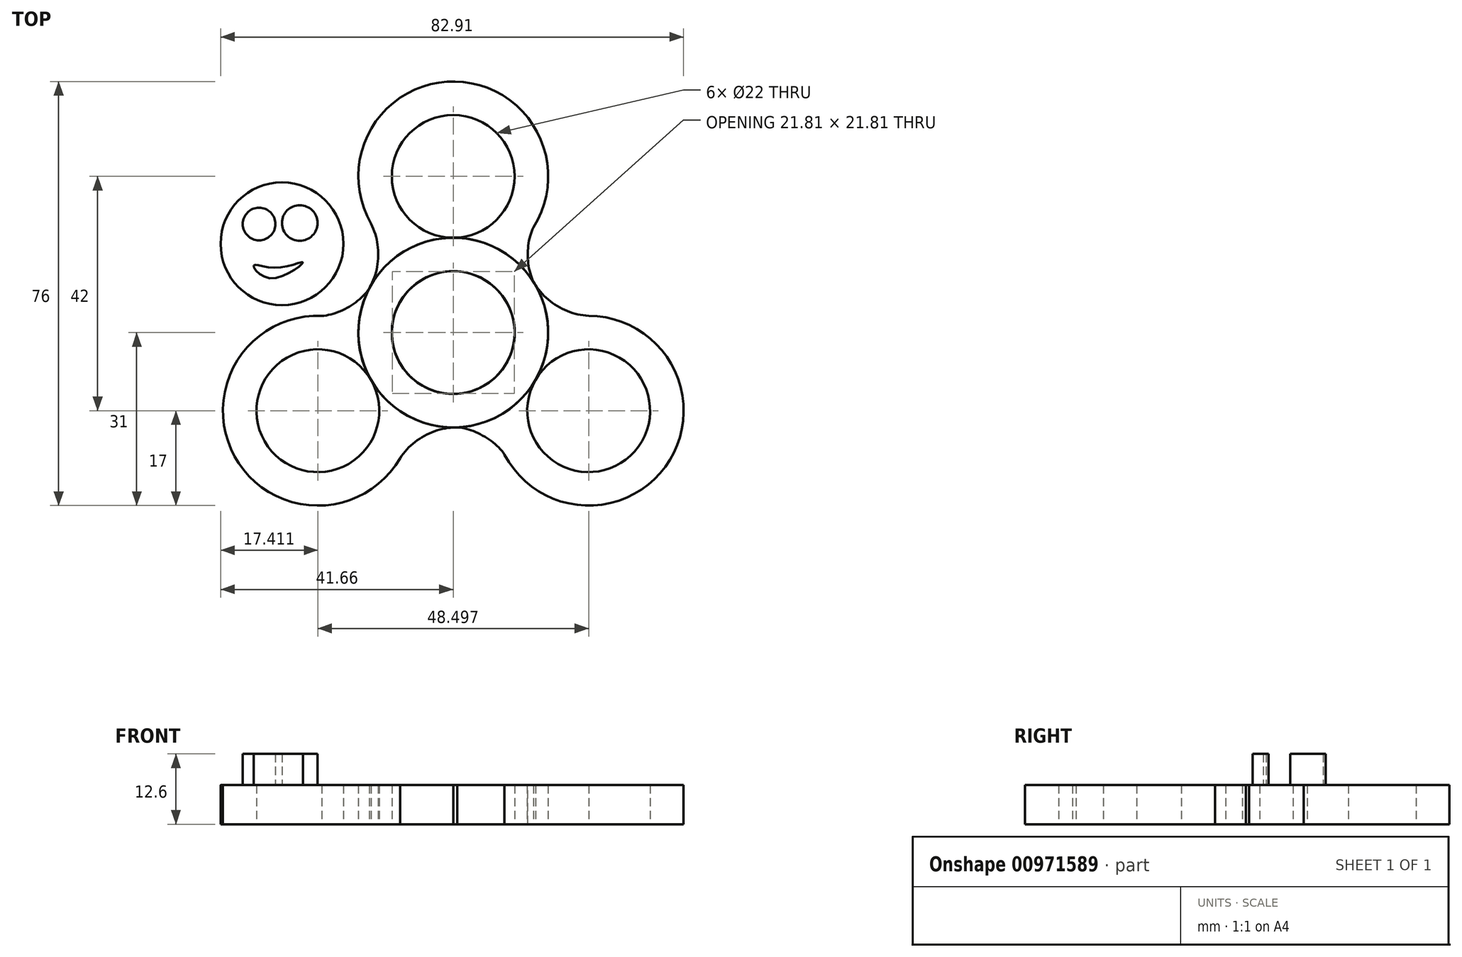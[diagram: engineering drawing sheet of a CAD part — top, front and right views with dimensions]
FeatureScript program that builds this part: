
annotation { "Feature Type Name" : "Feature", "Feature Type Description" : "" }
export const myFeature = defineFeature(function(context is Context, id is Id, definition is map)
    precondition{}
    {
        {
            var Q0;
            Q0=qCreatedBy(makeId("Top.planeOp"),FACE);
            var sketch = newSketch(context, id + "F0", { "sketchPlane" : qUnion([Q0])});
            skArc(sketch, "E0", {"start": v(-14.72, 8.5) * mm, "mid": v(0.36, -17) * mm, "end": v(14.35, 9.1) * mm});
            skArc(sketch, "E1", {"start": v(14.35, 18.9) * mm, "mid": v(0.36, 45) * mm, "end": v(-14.72, 19.5) * mm});
            skFitSpline(sketch, "E2", {"points": [v(-14.72, 19.5) * mm, v(-14.72, 8.5) * mm], "startDerivative": vector(5.17, -10.15) * mm, "endDerivative": vector(-5.17, -10.15) * mm});
            skFitSpline(sketch, "E3", {"points": [v(14.35, 18.9) * mm, v(14.35, 9.1) * mm], "startDerivative": vector(-4.06, -8.32) * mm, "endDerivative": vector(4.06, -8.32) * mm});
            skSolve(sketch);
        }
        {
            var Q0;
            Q0=makeQuery(id+"F0.imprint","IMPRINT",FACE,{"disambiguationData":[TD([[makeQuery(id+"F0.imprint","IMPRINT",EDGE,{"derivedFrom":sQuery(id+"F0.wireOp",EDGE,"E0")}),1.0]])]});
            extrude(context, id + "F1", {"entities" : qUnion([Q0]), "depth" : 7 * mm, "offsetDistance" : 25 * mm});
        }
        {
            var Q0;
            Q0=makeQuery(id+"F1.opExtrude","CAP_FACE",FACE,{"disambiguationData":[OSD([sQuery(id+"F0.wireOp",EDGE,"E0"),sQuery(id+"F0.wireOp",EDGE,"E1"),sQuery(id+"F0.wireOp",EDGE,"E2"),sQuery(id+"F0.wireOp",EDGE,"E3")])],"isStart":true});
            var sketch = newSketch(context, id + "F2", { "sketchPlane" : qUnion([Q0])});
            skCircle(sketch, "E4", {"center": v(0, 0) * mm, "radius": 11 * mm});
            skCircle(sketch, "E5", {"center": v(0, -28) * mm, "radius": 11 * mm});
            skSolve(sketch);
        }
        {
            var Q0;
            Q0 = qSketchRegion(id + "F2", true);
            extrude(context, id + "F3", {"entities" : qUnion([Q0]), "operationType" : NewBodyOperationType.REMOVE, "oppositeDirection" : true, "depth" : 25 * mm, "offsetDistance" : 25 * mm});
        }
        {
            var Q0;
            Q0=makeQuery(id+"F1.opExtrude","SWEPT_BODY",BODY,{"disambiguationData":[OSD([sQuery(id+"F0.wireOp",EDGE,"E0"),sQuery(id+"F0.wireOp",EDGE,"E1"),sQuery(id+"F0.wireOp",EDGE,"E2"),sQuery(id+"F0.wireOp",EDGE,"E3")])]});
            var Q1;
            Q1=makeQuery(id+"F3.boolean.opBoolean","INTERSECT",EDGE,{"derivedFrom":[makeQuery(id+"F1.opExtrude","CAP_FACE",FACE,{"disambiguationData":[OSD([sQuery(id+"F0.wireOp",EDGE,"E0"),sQuery(id+"F0.wireOp",EDGE,"E1"),sQuery(id+"F0.wireOp",EDGE,"E2"),sQuery(id+"F0.wireOp",EDGE,"E3")])],"isStart":false}),makeQuery(id+"F3.opExtrude","SWEPT_FACE",FACE,{"disambiguationData":[OSD([sQuery(id+"F2.wireOp",EDGE,"E4")])]})]});
            circularPattern(context, id + "F4", {"entities" : qUnion([Q0]), "axis" : qUnion([Q1]), "angle" : 360 * degree, "instanceCount" : 3, "equalSpace" : true});
        }
        {
            var Q0;
            Q0=qCreatedBy(makeId("Top.planeOp"),FACE);
            var sketch = newSketch(context, id + "F5", { "sketchPlane" : qUnion([Q0])});
            skCircle(sketch, "E6", {"center": v(-53.46, 44.5) * mm, "radius": 11 * mm});
            skSolve(sketch);
        }
        {
            var Q0;
            Q0=makeQuery(id+"F5.imprint","IMPRINT",FACE,{"disambiguationData":[TD([[makeQuery(id+"F5.imprint","IMPRINT",EDGE,{"derivedFrom":sQuery(id+"F5.wireOp",EDGE,"E6")}),1.0]])]});
            extrude(context, id + "F6", {"entities" : qUnion([Q0]), "depth" : 7 * mm, "offsetDistance" : 25 * mm});
        }
        {
            var Q0;
            Q0=makeQuery(id+"F6.opExtrude","CAP_FACE",FACE,{"disambiguationData":[OSD([sQuery(id+"F5.wireOp",EDGE,"E6")])],"isStart":false});
            var sketch = newSketch(context, id + "F7", { "sketchPlane" : qUnion([Q0])});
            skCircle(sketch, "E7", {"center": v(-57.57, 48.05) * mm, "radius": 2.92 * mm});
            skCircle(sketch, "E8", {"center": v(-50.3, 48.24) * mm, "radius": 3.2 * mm});
            skFitSpline(sketch, "E9", {"points": [v(-58.5, 40.59) * mm, v(-55.52, 38.35) * mm, v(-49.73, 41.15) * mm, v(-54.4, 40.21) * mm, v(-58.5, 40.59) * mm]});
            skSolve(sketch);
        }
        {
            var Q0;
            Q0=makeQuery(id+"F7.imprint","IMPRINT",FACE,{"disambiguationData":[TD([[makeQuery(id+"F7.imprint","IMPRINT",EDGE,{"derivedFrom":sQuery(id+"F7.wireOp",EDGE,"E7")}),1.0]])]});
            var Q1;
            Q1=makeQuery(id+"F7.imprint","IMPRINT",FACE,{"disambiguationData":[TD([[makeQuery(id+"F7.imprint","IMPRINT",EDGE,{"derivedFrom":sQuery(id+"F7.wireOp",EDGE,"E8")}),1.0]])]});
            var Q2;
            Q2=makeQuery(id+"F7.imprint","IMPRINT",FACE,{"disambiguationData":[TD([[makeQuery(id+"F7.imprint","IMPRINT",EDGE,{"derivedFrom":sQuery(id+"F7.wireOp",EDGE,"E9")}),1.0]])]});
            extrude(context, id + "F8", {"entities" : qUnion([Q0, Q1, Q2]), "operationType" : NewBodyOperationType.ADD, "depth" : 5.6 * mm, "offsetDistance" : 25 * mm});
        }
        {
            var Q0;
            Q0=makeQuery(id+"F6.opExtrude","SWEPT_BODY",BODY,{"disambiguationData":[OSD([sQuery(id+"F5.wireOp",EDGE,"E6")])]});
            transform(context, id + "F9", {"entities" : qUnion([Q0]), "transformType" : TransformType.TRANSLATION_3D, "dx" : 22.8 * mm, "dy" : -28.6 * mm, "dz" : 0 * mm, "makeCopy" : false});
        }
    });
